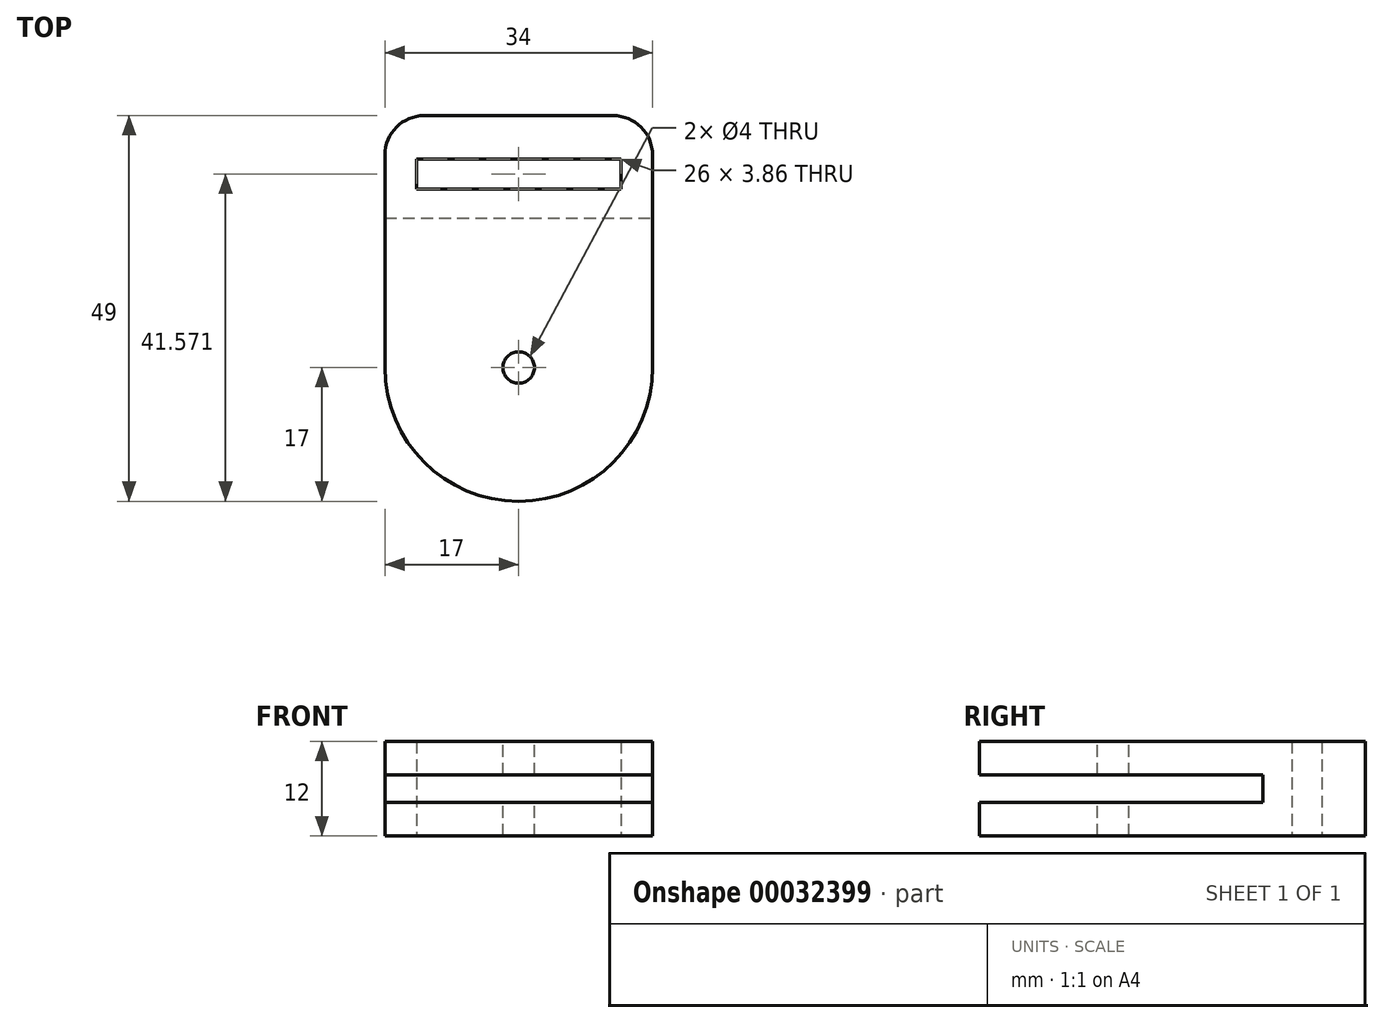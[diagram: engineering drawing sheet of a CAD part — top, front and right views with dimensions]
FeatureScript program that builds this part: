
annotation { "Feature Type Name" : "Feature", "Feature Type Description" : "" }
export const myFeature = defineFeature(function(context is Context, id is Id, definition is map)
    precondition{}
    {
        {
            var Q0;
            Q0=qCreatedBy(makeId("Front.planeOp"),FACE);
            var sketch = newSketch(context, id + "F0", { "sketchPlane" : qUnion([Q0])});
            skLineSegment(sketch, "E0.bottom", {"start": v(-17, 6) * mm, "end": v(17, 6) * mm});
            skLineSegment(sketch, "E0.top", {"start": v(-17, -6) * mm, "end": v(17, -6) * mm});
            skLineSegment(sketch, "E0.left", {"start": v(-17, 6) * mm, "end": v(-17, -6) * mm});
            skLineSegment(sketch, "E0.right", {"start": v(17, 6) * mm, "end": v(17, -6) * mm});
            skLineSegment(sketch, "E1", {"start": v(0, 6) * mm, "end": v(0, -6) * mm, "construction": true});
            skLineSegment(sketch, "E2", {"start": v(-17, 0) * mm, "end": v(17, 0) * mm, "construction": true});
            skSolve(sketch);
        }
        {
            var Q0;
            Q0 = qSketchRegion(id + "F0", true);
            extrude(context, id + "F1", {"entities" : qUnion([Q0]), "depth" : 15 * mm});
        }
        {
            var Q0;
            Q0=makeQuery(id+"F1.opExtrude","SWEPT_FACE",FACE,{"disambiguationData":[OSD([sQuery(id+"F0.wireOp",EDGE,"E0.top")])]});
            var sketch = newSketch(context, id + "F2", { "sketchPlane" : qUnion([Q0])});
            skLineSegment(sketch, "E3.rect.bottom", {"start": v(13, 9.36) * mm, "end": v(-13, 9.36) * mm});
            skLineSegment(sketch, "E3.rect.top", {"start": v(13, 5.5) * mm, "end": v(-13, 5.5) * mm});
            skLineSegment(sketch, "E3.rect.left", {"start": v(13, 9.36) * mm, "end": v(13, 5.5) * mm});
            skLineSegment(sketch, "E3.rect.right", {"start": v(-13, 9.36) * mm, "end": v(-13, 5.5) * mm});
            skPoint(sketch, "E3.rect.middle", {"position": v(0, 7.43) * mm});
            skSolve(sketch);
        }
        {
            var Q0;
            Q0 = qSketchRegion(id + "F2", true);
            extrude(context, id + "F3", {"entities" : qUnion([Q0]), "operationType" : NewBodyOperationType.REMOVE, "oppositeDirection" : true, "depth" : 25 * mm});
        }
        {
            var Q0;
            Q0=qCreatedBy(makeId("Top.planeOp"),FACE);
            var sketch = newSketch(context, id + "F4", { "sketchPlane" : qUnion([Q0])});
            skLineSegment(sketch, "E4.0", {"start": v(-17, -15) * mm, "end": v(17, -15) * mm, "construction": true});
            skLineSegment(sketch, "E5", {"start": v(0, -15) * mm, "end": v(0, -32) * mm, "construction": true});
            skPoint(sketch, "E5.endSnap0", {"position": v(0, -15) * mm});
            skArc(sketch, "E6", {"start": v(-17, -32) * mm, "mid": v(0, -49) * mm, "end": v(17, -32) * mm});
            skLineSegment(sketch, "E7", {"start": v(17, -15) * mm, "end": v(17, -32) * mm});
            skLineSegment(sketch, "E8", {"start": v(-17, -15) * mm, "end": v(-17, -32) * mm});
            skLineSegment(sketch, "E9", {"start": v(17, -15) * mm, "end": v(-17, -15) * mm});
            skSolve(sketch);
        }
        {
            var Q0;
            Q0=makeQuery(id+"F4.imprint","IMPRINT",FACE,{"disambiguationData":[TD([[makeQuery(id+"F4.imprint","IMPRINT",EDGE,{"derivedFrom":sQuery(id+"F4.wireOp",EDGE,"E6")}),1.0]])]});
            var Q1;
            Q1=makeQuery(id+"F1.opExtrude","SWEPT_FACE",FACE,{"disambiguationData":[OSD([sQuery(id+"F0.wireOp",EDGE,"E0.bottom")])]});
            var Q2;
            Q2=makeQuery(id+"F1.opExtrude","SWEPT_FACE",FACE,{"disambiguationData":[OSD([sQuery(id+"F0.wireOp",EDGE,"E0.top")])]});
            extrude(context, id + "F5", {"entities" : qUnion([Q0]), "operationType" : NewBodyOperationType.ADD, "endBound" : BoundingType.UP_TO_SURFACE, "endBoundEntityFace" : qUnion([Q1]), "depth" : 25 * mm, "hasSecondDirection" : true, "secondDirectionBound" : SecondDirectionBoundingType.UP_TO_SURFACE, "secondDirectionOppositeDirection" : true, "secondDirectionBoundEntityFace" : qUnion([Q2]), "secondDirectionDepth" : 25 * mm});
        }
        {
            var Q0;
            Q0=makeQuery(id+"F5.boolean.opBoolean","MERGE",FACE,{"derivedFrom":[makeQuery(id+"F1.opExtrude","SWEPT_FACE",FACE,{"disambiguationData":[OSD([sQuery(id+"F0.wireOp",EDGE,"E0.bottom")])]}),makeQuery(id+"F5.opExtrude","CAP_FACE",FACE,{"disambiguationData":[OSD([sQuery(id+"F4.wireOp",EDGE,"E6"),sQuery(id+"F4.wireOp",EDGE,"E7"),sQuery(id+"F4.wireOp",EDGE,"E8"),sQuery(id+"F4.wireOp",EDGE,"E9")])],"isStart":false})]});
            var sketch = newSketch(context, id + "F6", { "sketchPlane" : qUnion([Q0])});
            skArc(sketch, "E10.0", {"start": v(-17, -32) * mm, "mid": v(0, -49) * mm, "end": v(17, -32) * mm, "construction": true});
            skCircle(sketch, "E11", {"center": v(0, -32) * mm, "radius": 2 * mm});
            skSolve(sketch);
        }
        {
            var Q0;
            Q0 = qSketchRegion(id + "F6", true);
            extrude(context, id + "F7", {"entities" : qUnion([Q0]), "operationType" : NewBodyOperationType.REMOVE, "oppositeDirection" : true, "depth" : 25 * mm});
        }
        {
            var Q0;
            Q0=qCreatedBy(makeId("Top.planeOp"),FACE);
            var sketch = newSketch(context, id + "F8", { "sketchPlane" : qUnion([Q0])});
            skLineSegment(sketch, "E12", {"start": v(0, 0) * mm, "end": v(0, -13) * mm, "construction": true});
            skArc(sketch, "E13.0", {"start": v(-17, -32) * mm, "mid": v(0, -49) * mm, "end": v(17, -32) * mm});
            skLineSegment(sketch, "E14", {"start": v(0, -13) * mm, "end": v(17, -13) * mm});
            skLineSegment(sketch, "E15", {"start": v(17, -13) * mm, "end": v(17, -32) * mm});
            skLineSegment(sketch, "E16", {"start": v(-17, -32) * mm, "end": v(-17, -13) * mm});
            skLineSegment(sketch, "E17", {"start": v(-17, -13) * mm, "end": v(0, -13) * mm});
            skSolve(sketch);
        }
        {
            var Q0;
            Q0 = qSketchRegion(id + "F8", true);
            extrude(context, id + "F9", {"entities" : qUnion([Q0]), "operationType" : NewBodyOperationType.REMOVE, "oppositeDirection" : true, "depth" : 1.75 * mm, "hasSecondDirection" : true, "secondDirectionOppositeDirection" : false, "secondDirectionDepth" : 1.75 * mm});
        }
        {
            var Q0;
            Q0=makeQuery(id+"F1.opExtrude","CAP_EDGE",EDGE,{"disambiguationData":[OSD([sQuery(id+"F0.wireOp",EDGE,"E0.left")])],"isStart":true});
            var Q1;
            Q1=makeQuery(id+"F1.opExtrude","CAP_EDGE",EDGE,{"disambiguationData":[OSD([sQuery(id+"F0.wireOp",EDGE,"E0.right")])],"isStart":true});
            fillet(context, id + "F10", {"entities" : qUnion([Q0, Q1]), "radius" : 5 * mm, "tangentPropagation" : true, "allowEdgeOverflow" : false});
        }
    });
